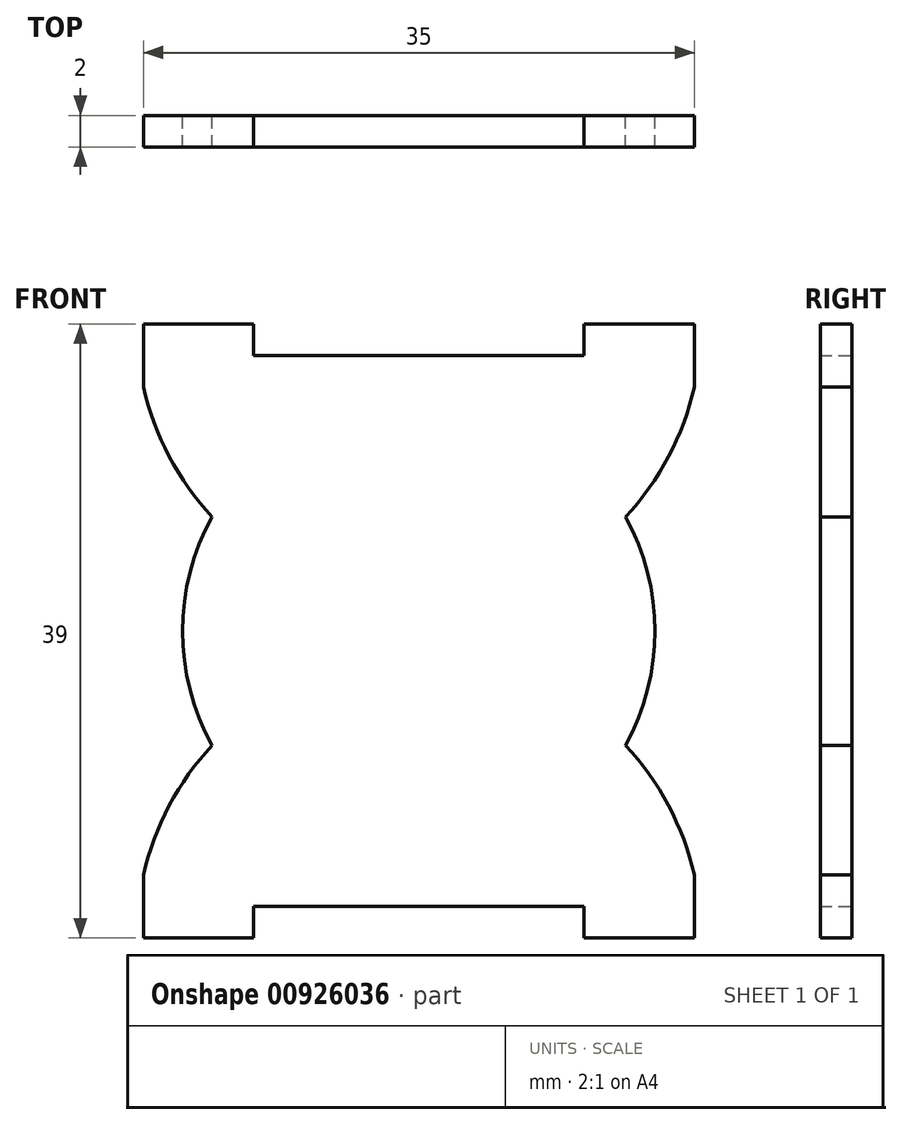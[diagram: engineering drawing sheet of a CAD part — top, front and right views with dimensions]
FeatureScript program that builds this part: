
annotation { "Feature Type Name" : "Feature", "Feature Type Description" : "" }
export const myFeature = defineFeature(function(context is Context, id is Id, definition is map)
    precondition{}
    {
        {
            var Q0;
            Q0=qCreatedBy(makeId("Front.planeOp"),FACE);
            var sketch = newSketch(context, id + "F0", { "sketchPlane" : qUnion([Q0])});
            skCircle(sketch, "E0", {"center": v(0, 0) * mm, "radius": 15 * mm});
            skLineSegment(sketch, "E1", {"start": v(17.5, 19.5) * mm, "end": v(10.5, 19.5) * mm});
            skLineSegment(sketch, "E2", {"start": v(10.5, 19.5) * mm, "end": v(10.5, 17.5) * mm});
            skLineSegment(sketch, "E3", {"start": v(10.5, 17.5) * mm, "end": v(-10.5, 17.5) * mm});
            skLineSegment(sketch, "E4", {"start": v(-10.5, 17.5) * mm, "end": v(-10.5, 19.5) * mm});
            skLineSegment(sketch, "E5", {"start": v(-10.5, 19.5) * mm, "end": v(-17.5, 19.5) * mm});
            skLineSegment(sketch, "E6", {"start": v(-17.5, 19.5) * mm, "end": v(-17.5, 15.5) * mm});
            skArc(sketch, "E7", {"start": v(-17.5, 15.5) * mm, "mid": v(0, 1.55) * mm, "end": v(17.5, 15.5) * mm});
            skLineSegment(sketch, "E8", {"start": v(17.5, 19.5) * mm, "end": v(17.5, 15.5) * mm});
            skPoint(sketch, "E9", {"position": v(0, 17.5) * mm});
            skLineSegment(sketch, "E10.MirrorCS", {"start": v(-10.5, -19.5) * mm, "end": v(-17.5, -19.5) * mm});
            skLineSegment(sketch, "E11.MirrorCS", {"start": v(-10.5, -17.5) * mm, "end": v(-10.5, -19.5) * mm});
            skLineSegment(sketch, "E12.MirrorCS", {"start": v(10.5, -17.5) * mm, "end": v(-10.5, -17.5) * mm});
            skLineSegment(sketch, "E13.MirrorCS", {"start": v(10.5, -19.5) * mm, "end": v(10.5, -17.5) * mm});
            skLineSegment(sketch, "E14.MirrorCS", {"start": v(17.5, -19.5) * mm, "end": v(10.5, -19.5) * mm});
            skLineSegment(sketch, "E15.MirrorCS", {"start": v(17.5, -19.5) * mm, "end": v(17.5, -15.5) * mm});
            skArc(sketch, "E16.MirrorCS", {"start": v(-17.5, -15.5) * mm, "mid": v(0, -1.55) * mm, "end": v(17.5, -15.5) * mm});
            skLineSegment(sketch, "E17.MirrorCS", {"start": v(-17.5, -19.5) * mm, "end": v(-17.5, -15.5) * mm});
            skSolve(sketch);
        }
        {
            var Q0;
            Q0 = qSketchRegion(id + "F0", true);
            extrude(context, id + "F1", {"entities" : qUnion([Q0]), "depth" : 2 * mm, "offsetDistance" : 25 * mm});
        }
    });
